# Revit family: 9th Avenue
name_source: partatom
category: Furniture
units: mm (PartAtom-declared; Revit-internal decimal feet)

## family parameters
Always vertical = Yes
Cut with Voids When Loaded = No
OmniClass Number = 23.40.20.00
OmniClass Title = General Furniture and Specialties
Room Calculation Point = No
Shared = No
Work Plane-Based = No

## types (6) — shared parameters
Default Elevation = 0"
Depth = 34"

## per-type parameters (varying)
| type | Cushion 2 | Cushion 3 | Cushion Width | Furniture Geometry | Ottoman | Ottoman Width | Seat Depth | Seat Height | Seat Width |
| Chair | No | No | 20" | Yes | No | 20" | 20" | 19" | 20" |
| Sofa | Yes | Yes | 22" | Yes | No | 20" | 22" | 20" | 66" |
| Loveseat | Yes | No | 22" | Yes | No | 20" | 22" | 20" | 44" |
| Ottoman | No | No | 20" | No | Yes | 20" | 20" | 19" | 20" |
| Wide Chair | No | No | 22" | Yes | No | 20" | 20" | 19" | 22" |
| Wide Ottoman | No | No | 22" | No | Yes | 22" | 20" | 19" | 22" |

## geometry (parser evidence)
native form markers: Sweep x11
no freeform markers — native parametric forms only
